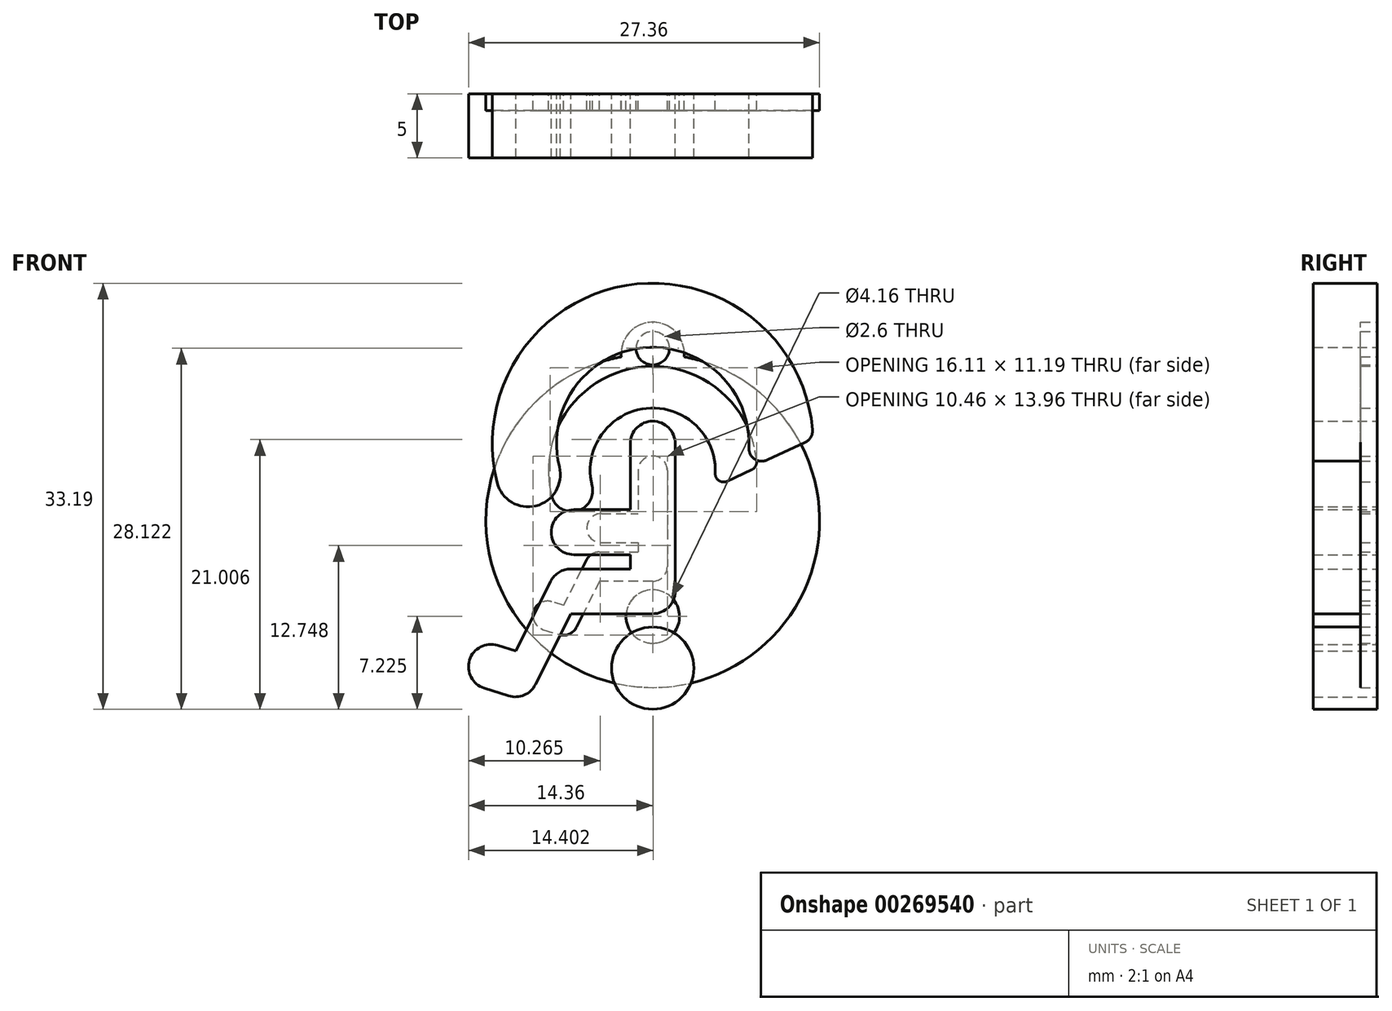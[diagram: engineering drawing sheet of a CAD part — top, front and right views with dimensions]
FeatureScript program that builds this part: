
annotation { "Feature Type Name" : "Feature", "Feature Type Description" : "" }
export const myFeature = defineFeature(function(context is Context, id is Id, definition is map)
    precondition{}
    {
        {
            var Q0;
            Q0=qCreatedBy(makeId("Front.planeOp"),FACE);
            var sketch = newSketch(context, id + "F0", { "sketchPlane" : qUnion([Q0])});
            skArc(sketch, "E0", {"start": v(-3.77, 19.64) * mm, "mid": v(0, -20) * mm, "end": v(3.77, 19.64) * mm});
            skArc(sketch, "E1", {"start": v(12.45, 7.1) * mm, "mid": v(-2.07, 18.33) * mm, "end": v(-12.13, 2.97) * mm});
            skArc(sketch, "E2", {"start": v(7.5, 5.67) * mm, "mid": v(-0.75, 13.46) * mm, "end": v(-7.28, 4.18) * mm});
            skArc(sketch, "E3", {"start": v(-12.13, 2.97) * mm, "mid": v(-9.1, 1.15) * mm, "end": v(-7.28, 4.18) * mm});
            skLineSegment(sketch, "E4", {"start": v(8.91, 4.72) * mm, "end": v(11.88, 6.1) * mm});
            skArc(sketch, "E5.trimOffspring", {"start": v(3.77, 19.64) * mm, "mid": v(0, 23.79) * mm, "end": v(-3.77, 19.64) * mm});
            skPoint(sketch, "E6.visualSharp", {"position": v(7.2, 3.93) * mm});
            skArc(sketch, "E6.filletArc", {"start": v(7.5, 5.67) * mm, "mid": v(7.94, 4.8) * mm, "end": v(8.91, 4.72) * mm});
            skPoint(sketch, "E7.visualSharp", {"position": v(12.5, 6.4) * mm});
            skArc(sketch, "E7.filletArc", {"start": v(11.88, 6.1) * mm, "mid": v(12.32, 6.51) * mm, "end": v(12.45, 7.1) * mm});
            skArc(sketch, "E8", {"start": v(1.75, 6) * mm, "mid": v(0, 7.75) * mm, "end": v(-1.75, 6) * mm});
            skArc(sketch, "E9", {"start": v(0, -7.26) * mm, "mid": v(1.24, -6.74) * mm, "end": v(1.75, -5.5) * mm});
            skArc(sketch, "E10", {"start": v(-6.16, 0.85) * mm, "mid": v(-7.91, -0.9) * mm, "end": v(-6.16, -2.65) * mm});
            skArc(sketch, "E11", {"start": v(-6.39, -3.76) * mm, "mid": v(-7.3, -4.02) * mm, "end": v(-7.95, -4.72) * mm});
            skArc(sketch, "E12", {"start": v(-11.23, -13.65) * mm, "mid": v(-10.02, -13.59) * mm, "end": v(-9.14, -12.76) * mm});
            skArc(sketch, "E13", {"start": v(-12.09, -9.71) * mm, "mid": v(-14.28, -10.86) * mm, "end": v(-13.13, -13.06) * mm});
            skLineSegment(sketch, "E14", {"start": v(-1.75, 6) * mm, "end": v(-1.75, 0.85) * mm});
            skLineSegment(sketch, "E15", {"start": v(1.75, 6) * mm, "end": v(1.75, -5.5) * mm});
            skLineSegment(sketch, "E16", {"start": v(0, -7.26) * mm, "end": v(-6.39, -7.26) * mm});
            skLineSegment(sketch, "E17", {"start": v(-6.39, -7.26) * mm, "end": v(-9.14, -12.76) * mm});
            skLineSegment(sketch, "E18", {"start": v(-10.67, -10.15) * mm, "end": v(-12.09, -9.71) * mm});
            skLineSegment(sketch, "E19", {"start": v(-13.13, -13.06) * mm, "end": v(-11.23, -13.65) * mm});
            skLineSegment(sketch, "E20", {"start": v(-10.67, -10.15) * mm, "end": v(-7.95, -4.72) * mm});
            skLineSegment(sketch, "E21", {"start": v(-6.39, -3.76) * mm, "end": v(-1.75, -3.76) * mm});
            skLineSegment(sketch, "E22", {"start": v(-6.16, -2.65) * mm, "end": v(-1.75, -2.65) * mm});
            skLineSegment(sketch, "E23", {"start": v(-6.16, 0.85) * mm, "end": v(-1.75, 0.85) * mm});
            skCircle(sketch, "E24", {"center": v(0, -11.49) * mm, "radius": 3.2 * mm});
            skPoint(sketch, "E25.orphan", {"position": v(-1.75, -5.5) * mm});
            skLineSegment(sketch, "E26", {"start": v(-1.75, -2.65) * mm, "end": v(-1.75, -3.76) * mm});
            skCircle(sketch, "E27", {"center": v(0, 20.66) * mm, "radius": 2 * mm});
            skSolve(sketch);
        }
        {
            var Q0;
            Q0=makeQuery(id+"F0.imprint","IMPRINT",FACE,{"disambiguationData":[TD([[makeQuery(id+"F0.imprint","IMPRINT",EDGE,{"derivedFrom":sQuery(id+"F0.wireOp",EDGE,"E1")}),1.0]])]});
            var Q1;
            Q1=makeQuery(id+"F0.imprint","IMPRINT",FACE,{"disambiguationData":[TD([[makeQuery(id+"F0.imprint","IMPRINT",EDGE,{"derivedFrom":sQuery(id+"F0.wireOp",EDGE,"E8")}),1.0]])]});
            var Q2;
            Q2=makeQuery(id+"F0.imprint","IMPRINT",FACE,{"disambiguationData":[TD([[makeQuery(id+"F0.imprint","IMPRINT",EDGE,{"derivedFrom":sQuery(id+"F0.wireOp",EDGE,"E24")}),1.0]])]});
            extrude(context, id + "F1", {"entities" : qUnion([Q0, Q1, Q2]), "depth" : 5 * mm});
        }
        {
            var Q0;
            Q0=makeQuery(id+"F0.imprint","IMPRINT",FACE,{"disambiguationData":[TD([[makeQuery(id+"F0.imprint","IMPRINT",EDGE,{"derivedFrom":sQuery(id+"F0.wireOp",EDGE,"E1")}),-1.0]])]});
            var Q1;
            {var subQ0=sQuery(id+"F0.wireOp",EDGE,"E5.trimOffspring");Q1=makeQuery(id+"F0.imprint","IMPRINT",FACE,{"disambiguationData":[TD([[makeQuery(id+"F0.imprint","IMPRINT",EDGE,{"derivedFrom":subQ0}),1.0]])]});}
            extrude(context, id + "F2", {"entities" : qUnion([Q0, Q1]), "depth" : 2 * mm});
        }
        {
            var Q0;
            Q0=makeQuery(id+"F2.opExtrude","SWEPT_BODY",BODY,{"disambiguationData":[OSD([sQuery(id+"F0.wireOp",EDGE,"E0"),sQuery(id+"F0.wireOp",EDGE,"E1"),sQuery(id+"F0.wireOp",EDGE,"E2"),sQuery(id+"F0.wireOp",EDGE,"E3"),sQuery(id+"F0.wireOp",EDGE,"E4"),sQuery(id+"F0.wireOp",EDGE,"E5.trimOffspring"),sQuery(id+"F0.wireOp",EDGE,"E6.filletArc"),sQuery(id+"F0.wireOp",EDGE,"E7.filletArc"),sQuery(id+"F0.wireOp",EDGE,"E8"),sQuery(id+"F0.wireOp",EDGE,"E9"),sQuery(id+"F0.wireOp",EDGE,"E10"),sQuery(id+"F0.wireOp",EDGE,"E11"),sQuery(id+"F0.wireOp",EDGE,"E12"),sQuery(id+"F0.wireOp",EDGE,"E13"),sQuery(id+"F0.wireOp",EDGE,"E14"),sQuery(id+"F0.wireOp",EDGE,"E15"),sQuery(id+"F0.wireOp",EDGE,"E16"),sQuery(id+"F0.wireOp",EDGE,"E17"),sQuery(id+"F0.wireOp",EDGE,"E18"),sQuery(id+"F0.wireOp",EDGE,"E19"),sQuery(id+"F0.wireOp",EDGE,"E20"),sQuery(id+"F0.wireOp",EDGE,"E21"),sQuery(id+"F0.wireOp",EDGE,"E22"),sQuery(id+"F0.wireOp",EDGE,"E23"),sQuery(id+"F0.wireOp",EDGE,"E24"),sQuery(id+"F0.wireOp",EDGE,"E26")])]});
            var Q1;
            Q1=sQuery(id+"F0.wireOp",VERTEX,"E0.center");
            transform(context, id + "F3", {"entities" : qUnion([Q0]), "transformType" : TransformType.SCALE_UNIFORMLY, "scale" : .65, "scalePoint" : qUnion([Q1]), "makeCopy" : false});
        }
    });
